# Revit family: Screens-Beam_Mounted-Teknion-JNSFGB_Floor_Screen-R20161
name_source: partatom
category: Furniture
revit_build: Autodesk Revit Architecture 2016 (Build: 20150714_1515(x64)
units: mm (PartAtom-declared; Revit-internal decimal feet)

## family parameters
Always vertical = Yes
Cut with Voids When Loaded = No
OmniClass Number = 23.40.70.14.64.21
OmniClass Title = Systems Furniture
Room Calculation Point = No
Shared = Yes
Work Plane-Based = No

## types (4) — shared parameters
Assembly Code = E2020200
Manufacturer = Teknion
Manufacturer Fax = 416.661.4586
Product Documentation Link = https://www.teknion.com
Product Line = Expansion Cityline
Product Page URL = https://www.teknion.com
Series = Expansion Cityline
Sustainability Data = https://www.teknion.com
URL = www.teknion.com
Unit Weight URL = http://www.teknion.com
Warranty = http://www.teknion.com

## per-type parameters (varying)
| type | Both Sides - Width Extension | Description | Left Offset | Model | Right Offset |
| Standard Width | No | Floor Screen with Glass – Beam-Mounted, Standard Width | 0 " | JNSFGB___S_ | 0 " |
| Both Sides Width Extension | Yes | Floor Screen with Glass – Beam-Mounted, Both Sides Width Extension | 1.016 " | JNSFGB___B_ | 1.016 " |
| One Side - Left Width Extension | No | Floor Screen with Glass – Beam-Mounted, One Side - Left Width Extension | 1.016 " | JNSFGB___L_ | 0 " |
| One Side - Right Width Extension | No | Floor Screen with Glass – Beam-Mounted, One Side - Right Width Extension | 0 " | JNSFGB___R_ | 1.016 " |

type visibility flags (boolean, named after types; folded from table):
- Standard Width: Yes: Standard Width
- Both Sides Width Extension: Yes: (none)
- One Side - Left Width Extension: Yes: One Side - Left Width Extension
- One Side - Right Width Extension: Yes: One Side - Right Width Extension

## geometry (parser evidence)
native form markers: Sweep x2
no freeform markers — native parametric forms only
